# Revit family: REC-02_RFA
name_source: partatom
category: Aparatos sanitarios
units: mm (PartAtom-declared; Revit-internal decimal feet)

## family parameters
Activar corte en vistas = No
Anfitrión = Cara
Compartido = Sí
Corte con vacíos al cargar = No
Cota de conector redondo = Usar diámetro
Mantener orientación de anotación = No
Número OmniClass = 23.45.05.14.17
Punto de cálculo de habitación = Sí
Tipo de pieza = Normal
Título OmniClass = Showers

## types (1)
- REC-02
    Brass Chromed = Brass
    Comentarios de tipo = Regadera Cuadrada 8" con Sistema Anticalcáreo
    Descripción = Regadera para Baja, Media y Alta Presión con Sistema Anticalcáreo
    Elevación por defecto = 0.50"
    Fabricante = PROYECTA
    Imagen de tipo = REC-02.jpg
    Inlet Threads = ½" - 14 NPT
    Max. Working Pressure = 83.34 psi
    Min. Working Pressure = 2.84 psi
    Modelo = REC-02
    Total Height = 4.20"
    Total Length = 8.00"

## geometry (parser evidence)
native form markers: Sweep x6
no freeform markers — native parametric forms only
